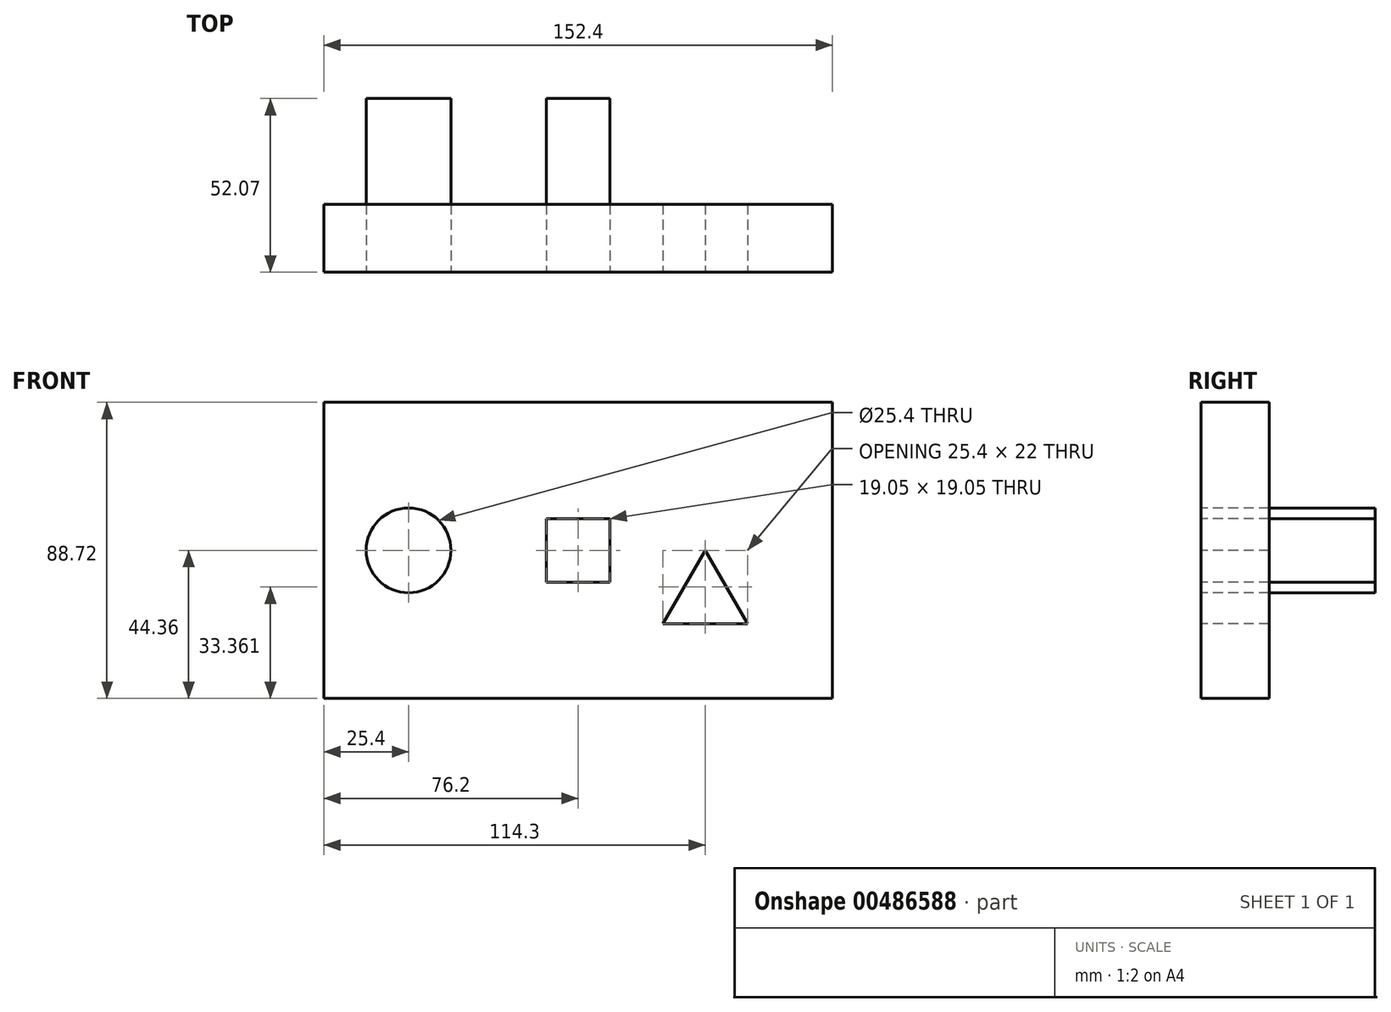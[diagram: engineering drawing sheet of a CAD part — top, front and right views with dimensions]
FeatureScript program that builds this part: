
annotation { "Feature Type Name" : "Feature", "Feature Type Description" : "" }
export const myFeature = defineFeature(function(context is Context, id is Id, definition is map)
    precondition{}
    {
        {
            var Q0;
            Q0=qCreatedBy(makeId("Front.planeOp"),FACE);
            var sketch = newSketch(context, id + "F0", { "sketchPlane" : qUnion([Q0])});
            skLineSegment(sketch, "E0", {"start": v(44.45, 0) * mm, "end": v(44.45, -44.36) * mm});
            skLineSegment(sketch, "E1", {"start": v(44.45, -44.36) * mm, "end": v(44.45, 0) * mm});
            skLineSegment(sketch, "E2", {"start": v(44.45, 44.36) * mm, "end": v(44.45, 0) * mm});
            skLineSegment(sketch, "E3", {"start": v(44.45, 44.36) * mm, "end": v(-107.95, 44.36) * mm});
            skLineSegment(sketch, "E4.top", {"start": v(-107.95, -44.36) * mm, "end": v(44.45, -44.36) * mm});
            skLineSegment(sketch, "E4.left", {"start": v(-107.95, 44.36) * mm, "end": v(-107.95, -44.36) * mm});
            skLineSegment(sketch, "E4.right", {"start": v(44.45, 44.54) * mm, "end": v(44.45, -44.36) * mm});
            skLineSegment(sketch, "E5", {"start": v(0, 0) * mm, "end": v(6.35, 0) * mm});
            skLineSegment(sketch, "E6", {"start": v(6.35, 0) * mm, "end": v(19.05, -22) * mm});
            skLineSegment(sketch, "E7", {"start": v(-6.35, -22) * mm, "end": v(6.35, 0) * mm});
            skLineSegment(sketch, "E8", {"start": v(-6.35, -22) * mm, "end": v(19.05, -22) * mm});
            skLineSegment(sketch, "E9.bottom", {"start": v(-22.23, 9.53) * mm, "end": v(-41.27, 9.53) * mm});
            skLineSegment(sketch, "E9.top", {"start": v(-22.23, -9.52) * mm, "end": v(-41.27, -9.52) * mm});
            skLineSegment(sketch, "E9.left", {"start": v(-22.23, 9.53) * mm, "end": v(-22.23, -9.53) * mm});
            skLineSegment(sketch, "E9.right", {"start": v(-41.27, 9.53) * mm, "end": v(-41.27, -9.53) * mm});
            skPoint(sketch, "E9.middle", {"position": v(-31.75, 0) * mm});
            skCircle(sketch, "E10", {"center": v(-82.55, 0) * mm, "radius": 12.7 * mm});
            skLineSegment(sketch, "E11", {"start": v(-31.75, 0) * mm, "end": v(0, 0) * mm});
            skLineSegment(sketch, "E12", {"start": v(-31.75, 0) * mm, "end": v(-82.55, 0) * mm});
            skPoint(sketch, "E13", {"position": v(0, -44.36) * mm});
            skLineSegment(sketch, "E14", {"start": v(0, -44.36) * mm, "end": v(44.45, -44.36) * mm});
            skSolve(sketch);
        }
        {
            var Q0;
            {var subQ0=sQuery(id+"F0.wireOp",EDGE,"E3");Q0=makeQuery(id+"F0.imprint","IMPRINT",FACE,{"disambiguationData":[TD([[makeQuery(id+"F0.imprint","IMPRINT",EDGE,{"derivedFrom":subQ0}),1.0]])]});}
            extrude(context, id + "F1", {"entities" : qUnion([Q0]), "oppositeDirection" : true, "depth" : 20.32 * mm});
        }
        {
            var Q0;
            Q0=makeQuery(id+"F0.imprint","IMPRINT",FACE,{"disambiguationData":[TD([[makeQuery(id+"F0.imprint","IMPRINT",EDGE,{"derivedFrom":sQuery(id+"F0.wireOp",EDGE,"E10")}),1.0]])]});
            var Q1;
            Q1=makeQuery(id+"F0.imprint","IMPRINT",FACE,{"disambiguationData":[TD([[makeQuery(id+"F0.imprint","IMPRINT",EDGE,{"derivedFrom":sQuery(id+"F0.wireOp",EDGE,"E9.bottom")}),1.0]])]});
            var Q2;
            {var subQ6=sQuery(id+"F0.wireOp",EDGE,"E9.top");Q2=makeQuery(id+"F0.imprint","IMPRINT",FACE,{"disambiguationData":[TD([[makeQuery(id+"F0.imprint","IMPRINT",EDGE,{"derivedFrom":subQ6}),-1.0]])]});}
            extrude(context, id + "F2", {"entities" : qUnion([Q0, Q1, Q2]), "oppositeDirection" : true, "depth" : 52.07 * mm});
        }
    });
